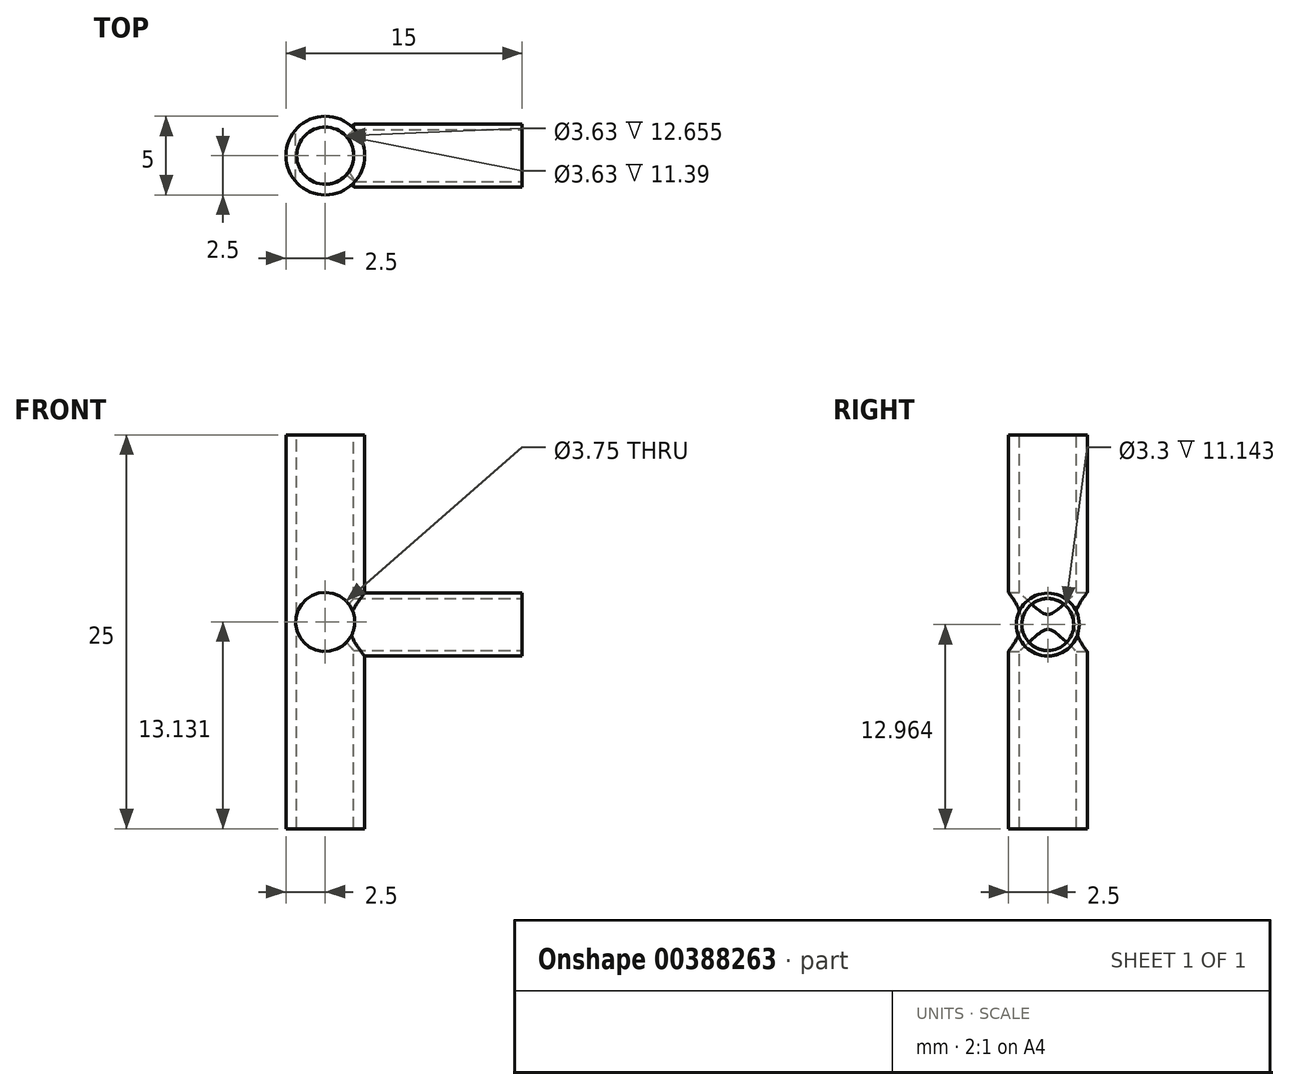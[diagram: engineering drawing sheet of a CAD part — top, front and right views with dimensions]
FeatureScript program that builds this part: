
annotation { "Feature Type Name" : "Feature", "Feature Type Description" : "" }
export const myFeature = defineFeature(function(context is Context, id is Id, definition is map)
    precondition{}
    {
        {
            var Q0;
            Q0=qCreatedBy(makeId("Top.planeOp"),FACE);
            var sketch = newSketch(context, id + "F0", { "sketchPlane" : qUnion([Q0])});
            skCircle(sketch, "E0", {"center": v(0, 0) * mm, "radius": 2.5 * mm});
            skSolve(sketch);
        }
        {
            var Q0;
            Q0 = qSketchRegion(id + "F0", true);
            extrude(context, id + "F1", {"entities" : qUnion([Q0]), "depth" : 25 * mm});
        }
        {
            var Q0;
            Q0=makeQuery(id+"F1.opExtrude","CAP_FACE",FACE,{"disambiguationData":[OSD([sQuery(id+"F0.wireOp",EDGE,"E0")])],"isStart":false});
            var sketch = newSketch(context, id + "F2", { "sketchPlane" : qUnion([Q0])});
            skCircle(sketch, "E1", {"center": v(0, 0) * mm, "radius": 1.81 * mm});
            skSolve(sketch);
        }
        {
            var Q0;
            Q0=qCreatedBy(makeId("Right.planeOp"),FACE);
            var sketch = newSketch(context, id + "F3", { "sketchPlane" : qUnion([Q0])});
            skCircle(sketch, "E2", {"center": v(0, 12.96) * mm, "radius": 2 * mm});
            skSolve(sketch);
        }
        {
            var Q0;
            Q0 = qSketchRegion(id + "F3", true);
            extrude(context, id + "F4", {"entities" : qUnion([Q0]), "operationType" : NewBodyOperationType.ADD, "depth" : 12.5 * mm});
        }
        {
            var Q0;
            Q0=makeQuery(id+"F4.opExtrude","CAP_FACE",FACE,{"disambiguationData":[OSD([sQuery(id+"F3.wireOp",EDGE,"E2")])],"isStart":false});
            var sketch = newSketch(context, id + "F5", { "sketchPlane" : qUnion([Q0])});
            skCircle(sketch, "E3", {"center": v(0, 12.96) * mm, "radius": 1.65 * mm});
            skSolve(sketch);
        }
        {
            var Q0;
            Q0=makeQuery(id+"F5.imprint","IMPRINT",FACE,{"disambiguationData":[TD([[makeQuery(id+"F5.imprint","IMPRINT",EDGE,{"derivedFrom":sQuery(id+"F5.wireOp",EDGE,"E3")}),1.0]])]});
            var Q1;
            Q1=sQuery(id+"F5.wireOp",EDGE,"E3");
            extrude(context, id + "F6", {"entities" : qUnion([Q0]), "operationType" : NewBodyOperationType.REMOVE, "surfaceEntities" : qUnion([Q1]), "oppositeDirection" : true, "depth" : 12 * mm});
        }
        {
            var Q0;
            Q0=makeQuery(id+"F2.imprint","IMPRINT",FACE,{"disambiguationData":[TD([[makeQuery(id+"F2.imprint","IMPRINT",EDGE,{"derivedFrom":sQuery(id+"F2.wireOp",EDGE,"E1")}),1.0]])]});
            var Q1;
            Q1=sQuery(id+"F2.wireOp",EDGE,"E1");
            extrude(context, id + "F7", {"entities" : qUnion([Q0]), "operationType" : NewBodyOperationType.REMOVE, "surfaceEntities" : qUnion([Q1]), "endBound" : BoundingType.THROUGH_ALL, "oppositeDirection" : true, "depth" : 25 * mm});
        }
        {
            var Q0;
            Q0=qCreatedBy(makeId("Front.planeOp"),FACE);
            var sketch = newSketch(context, id + "F8", { "sketchPlane" : qUnion([Q0])});
            skCircle(sketch, "E4", {"center": v(0, 13.13) * mm, "radius": 1.88 * mm});
            skSolve(sketch);
        }
        {
            var Q0;
            Q0 = qSketchRegion(id + "F8", true);
            extrude(context, id + "F9", {"entities" : qUnion([Q0]), "operationType" : NewBodyOperationType.REMOVE, "endBound" : BoundingType.THROUGH_ALL, "depth" : 25 * mm});
        }
        {
            var Q0;
            Q0 = qSketchRegion(id + "F8", true);
            var Q1;
            Q1=sQuery(id+"F8.wireOp",EDGE,"E4");
            extrude(context, id + "F10", {"entities" : qUnion([Q0]), "operationType" : NewBodyOperationType.REMOVE, "surfaceEntities" : qUnion([Q1]), "endBound" : BoundingType.THROUGH_ALL, "oppositeDirection" : true, "depth" : 25 * mm});
        }
    });
